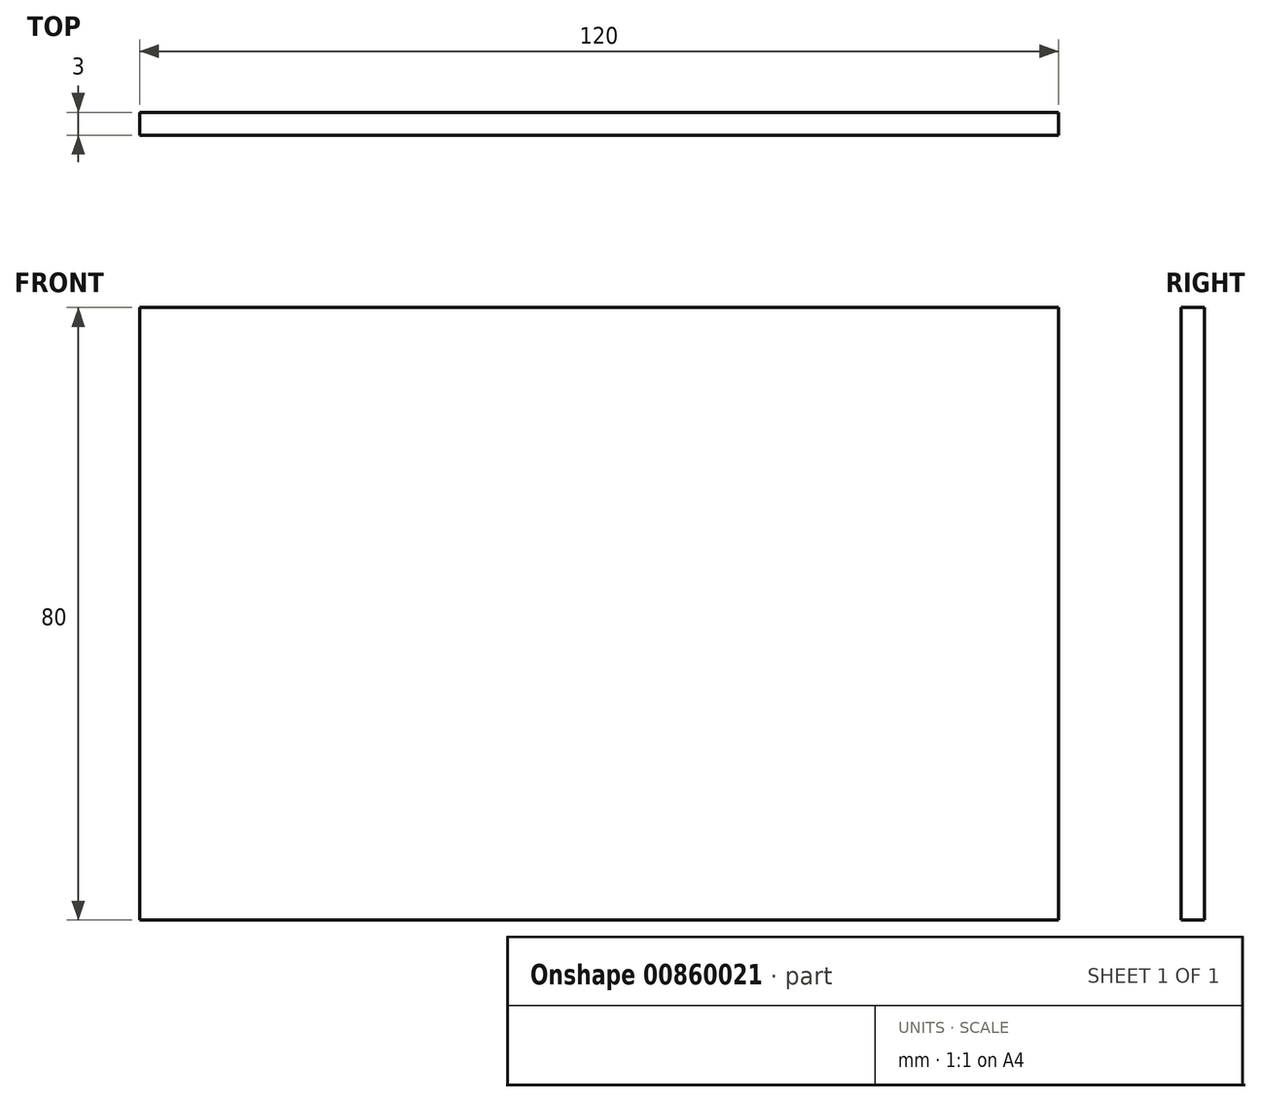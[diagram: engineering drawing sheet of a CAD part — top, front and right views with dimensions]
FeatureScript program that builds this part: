
annotation { "Feature Type Name" : "Feature", "Feature Type Description" : "" }
export const myFeature = defineFeature(function(context is Context, id is Id, definition is map)
    precondition{}
    {
        {
            var Q0;
            Q0=qCreatedBy(makeId("Front.planeOp"),FACE);
            var sketch = newSketch(context, id + "F0", { "sketchPlane" : qUnion([Q0])});
            skLineSegment(sketch, "E0.bottom", {"start": v(60, 40) * mm, "end": v(-60, 40) * mm});
            skLineSegment(sketch, "E0.top", {"start": v(60, -40) * mm, "end": v(-60, -40) * mm});
            skLineSegment(sketch, "E0.left", {"start": v(60, 40) * mm, "end": v(60, -40) * mm});
            skLineSegment(sketch, "E0.right", {"start": v(-60, 40) * mm, "end": v(-60, -40) * mm});
            skPoint(sketch, "E0.middle", {"position": v(0, 0) * mm});
            skSolve(sketch);
        }
        {
            var Q0;
            Q0 = qSketchRegion(id + "F0", true);
            extrude(context, id + "F1", {"entities" : qUnion([Q0]), "depth" : 3 * mm, "offsetDistance" : 25 * mm});
        }
    });
